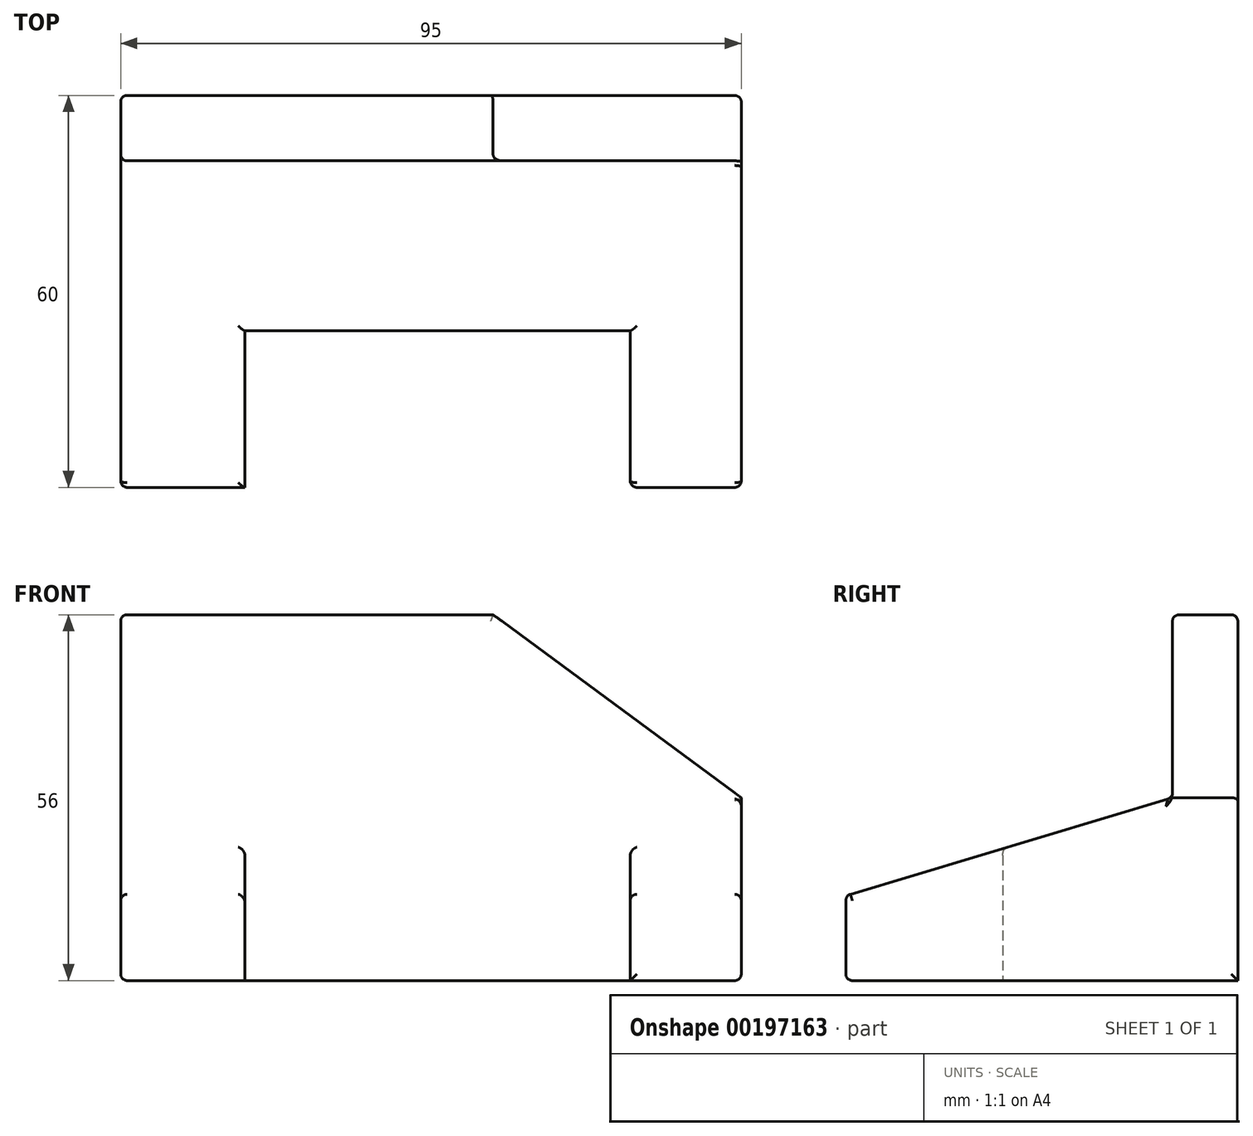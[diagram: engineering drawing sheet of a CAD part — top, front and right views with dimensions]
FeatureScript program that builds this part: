
annotation { "Feature Type Name" : "Feature", "Feature Type Description" : "" }
export const myFeature = defineFeature(function(context is Context, id is Id, definition is map)
    precondition{}
    {
        {
            var Q0;
            Q0=qCreatedBy(makeId("Right.planeOp"),FACE);
            var sketch = newSketch(context, id + "F0", { "sketchPlane" : qUnion([Q0])});
            skLineSegment(sketch, "E0", {"start": v(0, 0) * mm, "end": v(0, 28) * mm});
            skLineSegment(sketch, "E1", {"start": v(0, 28) * mm, "end": v(-10, 28) * mm});
            skLineSegment(sketch, "E2", {"start": v(0, 0) * mm, "end": v(-60, 0) * mm});
            skLineSegment(sketch, "E3", {"start": v(-60, 0) * mm, "end": v(-60, 13) * mm});
            skLineSegment(sketch, "E4", {"start": v(-60, 13) * mm, "end": v(-10, 28) * mm});
            skLineSegment(sketch, "E5.bottom", {"start": v(-10, 28) * mm, "end": v(0, 28) * mm});
            skLineSegment(sketch, "E5.top", {"start": v(-10, 56) * mm, "end": v(0, 56) * mm});
            skLineSegment(sketch, "E5.left", {"start": v(-10, 28) * mm, "end": v(-10, 56) * mm});
            skLineSegment(sketch, "E5.right", {"start": v(0, 28) * mm, "end": v(0, 56) * mm});
            skSolve(sketch);
        }
        {
            var Q0;
            Q0=qSketchRegion(id+"F0",true);
            extrude(context, id + "F1", {"entities" : qUnion([Q0]), "depth" : 95 * mm});
        }
        {
            var Q0;
            Q0=makeQuery(id+"F1.opExtrude","SWEPT_FACE",FACE,{"disambiguationData":[OSD([sQuery(id+"F0.wireOp",EDGE,"E5.left")])]});
            var sketch = newSketch(context, id + "F2", { "sketchPlane" : qUnion([Q0])});
            skLineSegment(sketch, "E6.bottom", {"start": v(0, 56) * mm, "end": v(57, 56) * mm});
            skLineSegment(sketch, "E6.top", {"start": v(0, 28) * mm, "end": v(57, 28) * mm});
            skLineSegment(sketch, "E6.left", {"start": v(0, 56) * mm, "end": v(0, 28) * mm});
            skLineSegment(sketch, "E6.right", {"start": v(57, 56) * mm, "end": v(57, 28) * mm});
            skLineSegment(sketch, "E7", {"start": v(57, 56) * mm, "end": v(95, 28) * mm});
            skSolve(sketch);
        }
        {
            var Q0;
            {var subQ0=sQuery(id+"F2.wireOp",EDGE,"E7");Q0=makeQuery(id+"F2.imprint","IMPRINT",FACE,{"disambiguationData":[TD([[makeQuery(id+"F2.imprint","IMPRINT",EDGE,{"derivedFrom":subQ0}),1.0]])]});}
            extrude(context, id + "F3", {"entities" : qUnion([Q0]), "operationType" : NewBodyOperationType.REMOVE, "oppositeDirection" : true, "depth" : 25 * mm});
        }
        {
            var Q0;
            Q0=makeQuery(id+"F1.opExtrude","SWEPT_FACE",FACE,{"disambiguationData":[OSD([sQuery(id+"F0.wireOp",EDGE,"E2")])]});
            var sketch = newSketch(context, id + "F4", { "sketchPlane" : qUnion([Q0])});
            skLineSegment(sketch, "E8.bottom", {"start": v(0, 60) * mm, "end": v(19, 60) * mm});
            skLineSegment(sketch, "E8.top", {"start": v(0, 36) * mm, "end": v(19, 36) * mm});
            skLineSegment(sketch, "E8.left", {"start": v(0, 60) * mm, "end": v(0, 36) * mm});
            skLineSegment(sketch, "E8.right", {"start": v(19, 60) * mm, "end": v(19, 36) * mm});
            skLineSegment(sketch, "E9.bottom", {"start": v(0, 60) * mm, "end": v(78, 60) * mm});
            skLineSegment(sketch, "E9.top", {"start": v(0, 36) * mm, "end": v(78, 36) * mm});
            skLineSegment(sketch, "E9.right", {"start": v(78, 60) * mm, "end": v(78, 36) * mm});
            skSolve(sketch);
        }
        {
            var Q0;
            {var subQ0=sQuery(id+"F4.wireOp",EDGE,"E8.right");Q0=makeQuery(id+"F4.imprint","IMPRINT",FACE,{"disambiguationData":[TD([[makeQuery(id+"F4.imprint","IMPRINT",EDGE,{"derivedFrom":subQ0}),1.0]])]});}
            extrude(context, id + "F5", {"entities" : qUnion([Q0]), "operationType" : NewBodyOperationType.REMOVE, "oppositeDirection" : true, "depth" : 25 * mm});
        }
        {
            var Q0;
            Q0=makeQuery(id+"F5.boolean.opBoolean","INTERSECT",EDGE,{"derivedFrom":[makeQuery(id+"F1.opExtrude","SWEPT_FACE",FACE,{"disambiguationData":[OSD([sQuery(id+"F0.wireOp",EDGE,"E4")])]}),makeQuery(id+"F5.opExtrude","SWEPT_FACE",FACE,{"disambiguationData":[OSD([sQuery(id+"F4.wireOp",EDGE,"E8.right")])]})]});
            var Q1;
            Q1=makeQuery(id+"F5.boolean.opBoolean","INTERSECT",EDGE,{"derivedFrom":[makeQuery(id+"F1.opExtrude","SWEPT_FACE",FACE,{"disambiguationData":[OSD([sQuery(id+"F0.wireOp",EDGE,"E4")])]}),makeQuery(id+"F5.opExtrude","SWEPT_FACE",FACE,{"disambiguationData":[OSD([sQuery(id+"F4.wireOp",EDGE,"E9.top")])]})]});
            var Q2;
            Q2=makeQuery(id+"F5.boolean.opBoolean","INTERSECT",EDGE,{"derivedFrom":[makeQuery(id+"F1.opExtrude","SWEPT_FACE",FACE,{"disambiguationData":[OSD([sQuery(id+"F0.wireOp",EDGE,"E4")])]}),makeQuery(id+"F5.opExtrude","SWEPT_FACE",FACE,{"disambiguationData":[OSD([sQuery(id+"F4.wireOp",EDGE,"E9.right")])]})]});
            var Q3;
            {var subQ0=sQuery(id+"F0.wireOp",EDGE,"E4");var subQ1=sQuery(id+"F0.wireOp",EDGE,"E3");Q3=makeQuery(id+"F5.boolean.opBoolean","SPLIT",EDGE,{"disambiguationData":[TD([makeQuery(id+"F5.opExtrude","SWEPT_FACE",FACE,{"disambiguationData":[OSD([sQuery(id+"F4.wireOp",EDGE,"E9.right")])]})])],"derivedFrom":makeQuery(id+"F1.opExtrude","SWEPT_EDGE",EDGE,{"disambiguationData":[OSD([subQ1,subQ0])]})});}
            var Q4;
            Q4=makeQuery(id+"F1.opExtrude","CAP_EDGE",EDGE,{"disambiguationData":[OSD([sQuery(id+"F0.wireOp",EDGE,"E4")])],"isStart":false});
            var Q5;
            {var subQ0=sQuery(id+"F0.wireOp",EDGE,"E4");var subQ1=sQuery(id+"F0.wireOp",EDGE,"E3");Q5=makeQuery(id+"F5.boolean.opBoolean","SPLIT",EDGE,{"disambiguationData":[TD([makeQuery(id+"F5.opExtrude","SWEPT_FACE",FACE,{"disambiguationData":[OSD([sQuery(id+"F4.wireOp",EDGE,"E8.right")])]})])],"derivedFrom":makeQuery(id+"F1.opExtrude","SWEPT_EDGE",EDGE,{"disambiguationData":[OSD([subQ1,subQ0])]})});}
            var Q6;
            Q6=makeQuery(id+"F1.opExtrude","CAP_EDGE",EDGE,{"disambiguationData":[OSD([sQuery(id+"F0.wireOp",EDGE,"E4")])],"isStart":true});
            fillet(context, id + "F6", {"entities" : qUnion([Q0, Q1, Q2, Q3, Q4, Q5, Q6]), "radius" : 1 * mm, "tangentPropagation" : true, "allowEdgeOverflow" : false});
        }
        {
            var Q0;
            Q0=makeQuery(id+"F1.opExtrude","SWEPT_EDGE",EDGE,{"disambiguationData":[OSD([sQuery(id+"F0.wireOp",EDGE,"E4"),sQuery(id+"F0.wireOp",EDGE,"E5.bottom"),sQuery(id+"F0.wireOp",EDGE,"E5.left")])]});
            var Q1;
            Q1=makeQuery(id+"F1.opExtrude","CAP_EDGE",EDGE,{"disambiguationData":[OSD([sQuery(id+"F0.wireOp",EDGE,"E5.left")])],"isStart":true});
            var Q2;
            Q2=makeQuery(id+"F1.opExtrude","SWEPT_EDGE",EDGE,{"disambiguationData":[OSD([sQuery(id+"F0.wireOp",EDGE,"E5.top"),sQuery(id+"F0.wireOp",EDGE,"E5.left")])]});
            var Q3;
            Q3=makeQuery(id+"F1.opExtrude","CAP_EDGE",EDGE,{"disambiguationData":[OSD([sQuery(id+"F0.wireOp",EDGE,"E5.top")])],"isStart":true});
            var Q4;
            Q4=makeQuery(id+"F1.opExtrude","CAP_EDGE",EDGE,{"disambiguationData":[OSD([sQuery(id+"F0.wireOp",EDGE,"E0"),sQuery(id+"F0.wireOp",EDGE,"E5.right")])],"isStart":true});
            var Q5;
            Q5=makeQuery(id+"F1.opExtrude","CAP_EDGE",EDGE,{"disambiguationData":[OSD([sQuery(id+"F0.wireOp",EDGE,"E2")])],"isStart":true});
            var Q6;
            Q6=makeQuery(id+"F1.opExtrude","CAP_EDGE",EDGE,{"disambiguationData":[OSD([sQuery(id+"F0.wireOp",EDGE,"E3")])],"isStart":true});
            var Q7;
            {var subQ0=sQuery(id+"F0.wireOp",EDGE,"E3");var subQ1=sQuery(id+"F0.wireOp",EDGE,"E2");Q7=makeQuery(id+"F5.boolean.opBoolean","SPLIT",EDGE,{"disambiguationData":[TD([makeQuery(id+"F5.opExtrude","SWEPT_FACE",FACE,{"disambiguationData":[OSD([sQuery(id+"F4.wireOp",EDGE,"E8.right")])]})])],"derivedFrom":makeQuery(id+"F1.opExtrude","SWEPT_EDGE",EDGE,{"disambiguationData":[OSD([subQ1,subQ0])]})});}
            var Q8;
            Q8=makeQuery(id+"F5.boolean.opBoolean","COPY",EDGE,{"derivedFrom":makeQuery(id+"F5.opExtrude","SWEPT_EDGE",EDGE,{"disambiguationData":[OSD([sQuery(id+"F4.wireOp",EDGE,"E8.right"),sQuery(id+"F4.wireOp",EDGE,"E9.bottom")])]})});
            var Q9;
            Q9=makeQuery(id+"F5.boolean.opBoolean","COPY",EDGE,{"derivedFrom":makeQuery(id+"F5.opExtrude","CAP_EDGE",EDGE,{"disambiguationData":[OSD([sQuery(id+"F4.wireOp",EDGE,"E8.right")])],"isStart":true})});
            var Q10;
            Q10=makeQuery(id+"F5.boolean.opBoolean","COPY",EDGE,{"derivedFrom":makeQuery(id+"F5.opExtrude","CAP_EDGE",EDGE,{"disambiguationData":[OSD([sQuery(id+"F4.wireOp",EDGE,"E9.top")])],"isStart":true})});
            var Q11;
            Q11=makeQuery(id+"F5.boolean.opBoolean","COPY",EDGE,{"derivedFrom":makeQuery(id+"F5.opExtrude","CAP_EDGE",EDGE,{"disambiguationData":[OSD([sQuery(id+"F4.wireOp",EDGE,"E9.right")])],"isStart":true})});
            var Q12;
            Q12=makeQuery(id+"F5.boolean.opBoolean","COPY",EDGE,{"derivedFrom":makeQuery(id+"F5.opExtrude","SWEPT_EDGE",EDGE,{"disambiguationData":[OSD([sQuery(id+"F0.wireOp",EDGE,"E2"),sQuery(id+"F0.wireOp",EDGE,"E3"),sQuery(id+"F4.wireOp",EDGE,"E9.bottom"),sQuery(id+"F4.wireOp",EDGE,"E9.right")])]})});
            var Q13;
            {var subQ0=sQuery(id+"F0.wireOp",EDGE,"E3");var subQ1=sQuery(id+"F0.wireOp",EDGE,"E2");Q13=makeQuery(id+"F5.boolean.opBoolean","SPLIT",EDGE,{"disambiguationData":[TD([makeQuery(id+"F5.opExtrude","SWEPT_FACE",FACE,{"disambiguationData":[OSD([sQuery(id+"F4.wireOp",EDGE,"E9.right")])]})])],"derivedFrom":makeQuery(id+"F1.opExtrude","SWEPT_EDGE",EDGE,{"disambiguationData":[OSD([subQ1,subQ0])]})});}
            var Q14;
            Q14=makeQuery(id+"F1.opExtrude","CAP_EDGE",EDGE,{"disambiguationData":[OSD([sQuery(id+"F0.wireOp",EDGE,"E3")])],"isStart":false});
            var Q15;
            Q15=makeQuery(id+"F1.opExtrude","CAP_EDGE",EDGE,{"disambiguationData":[OSD([sQuery(id+"F0.wireOp",EDGE,"E2")])],"isStart":false});
            var Q16;
            Q16=makeQuery(id+"F1.opExtrude","CAP_EDGE",EDGE,{"disambiguationData":[OSD([sQuery(id+"F0.wireOp",EDGE,"E0"),sQuery(id+"F0.wireOp",EDGE,"E5.right")])],"isStart":false});
            var Q17;
            Q17=makeQuery(id+"F3.boolean.opBoolean","INTERSECT",EDGE,{"derivedFrom":[makeQuery(id+"F1.opExtrude","SWEPT_FACE",FACE,{"disambiguationData":[OSD([sQuery(id+"F0.wireOp",EDGE,"E0"),sQuery(id+"F0.wireOp",EDGE,"E5.right")])]}),makeQuery(id+"F3.opExtrude","SWEPT_FACE",FACE,{"disambiguationData":[OSD([sQuery(id+"F2.wireOp",EDGE,"E7")])]})]});
            var Q18;
            Q18=makeQuery(id+"F1.opExtrude","SWEPT_EDGE",EDGE,{"disambiguationData":[OSD([sQuery(id+"F0.wireOp",EDGE,"E5.top"),sQuery(id+"F0.wireOp",EDGE,"E5.right")])]});
            fillet(context, id + "F7", {"entities" : qUnion([Q0, Q1, Q2, Q3, Q4, Q5, Q6, Q7, Q8, Q9, Q10, Q11, Q12, Q13, Q14, Q15, Q16, Q17, Q18]), "radius" : 1 * mm, "tangentPropagation" : true, "allowEdgeOverflow" : false});
        }
    });
